FCSTD DOCUMENT  (FreeCAD 0.18R4 (GitTag))
Label: stator2
License: All rights reserved
LicenseURL: http://en.wikipedia.org/wiki/All_rights_reserved
objects: Sketcher::SketchObject×3, PartDesign::Body×2, Spreadsheet::Sheet×1
note: 5 computed .brp shape members not serialized (recipe doc carries the construction recipe); baked Part::Feature solids carry a one-line shape summary decoded from their .brp

FEATURE [Spreadsheet::Sheet] Spreadsheet  label="Variables"
  cells = A2=slotNumber; B2(slotNumber)=7; A3=outerDiameter; B3(outerDiameter)=50.15; A4=innerDiameter; B4(innerDiameter)=10; A5=stackLength; B5(stackLength)=20; A6=stackingFactor; B6(stackingFactor)=0.95; A7=cuttingThickness; B7(cuttingThickness)=0.1; A8=skewAngle; B8(skewAngle)=0; A9=segmentAngle; B9(segmentAngle)==360 / slotNumber; A10=tipHeightReduction; B10(tipHeightReduction)=50; A11=toothThickness; B11(toothThickness)=3; A12=yokeThickness; B12(yokeThickness)=4; A13=tipHeight; B13(tipHeight)=0.8; A14=tipAngle; B14(tipAngle)=90; A15=openingLeft; B15(openingLeft)=3; A16=openingRight; B16(openingRight)=3; A17=slotIsolation; B17(slotIsolation)=0.5; A18=windingAngle; B18(windingAngle)=35; A19=heightRatio; B19(heightRatio)=45; A20=roundingRadii; B20(roundingRadii)=0.2
FEATURE [Sketcher::SketchObject] Sketch003  label="StatorSegment"
  MapMode = 5
  Support = -> [XY_Plane]
  expr: Constraints[82] = Variables.roundingRadii
  expr: Constraints[54] = Variables.innerDiameter / 2 + Variables.yokeThickness
  expr: Constraints[79] = Variables.roundingRadii
  expr: Constraints[21] = 90
  expr: Constraints[64] = Variables.roundingRadii
  expr: Constraints[76] = Variables.roundingRadii
  expr: Constraints[42] = Variables.tipAngle
  expr: Constraints[13] = Variables.innerDiameter / 2
  expr: Constraints[7] = Variables.tipHeight
  expr: Constraints[27] = 90
  expr: Constraints[41] = Variables.tipAngle
  expr: Constraints[22] = Variables.openingLeft
  expr: Constraints[14] = Variables.segmentAngle / 2
  expr: Constraints[4] = Variables.tipHeight * (1 - Variables.tipHeightReduction / 100)
  expr: Constraints[89] = Variables.tipHeight
  expr: Constraints[32] = Variables.openingRight
  expr: Constraints[71] = Variables.roundingRadii
  expr: Constraints[46] = Variables.toothThickness / 2
  expr: Constraints[0] = Variables.segmentAngle
  expr: Constraints[18] = Variables.outerDiameter / 2
  expr: Constraints[34] = Variables.tipHeight * (1 - Variables.tipHeightReduction / 100)
  sketch-geometry (36):
    g0: LineSegment [constr] StartX=0 StartY=0 StartZ=0 EndX=15.634 EndY=19.6044 EndZ=0
    g1: LineSegment [constr] StartX=0 StartY=0 StartZ=0 EndX=25.075 EndY=0 EndZ=0
    g2: LineSegment [constr] StartX=0 StartY=0 StartZ=0 EndX=22.5918 EndY=10.8796 EndZ=0
    g3: LineSegment [constr] StartX=8.5045 StartY=23.7788 StartZ=0 EndX=21.2901 EndY=13.5825 EndZ=0
    g4: LineSegment [constr] StartX=21.2901 StartY=13.5825 StartZ=0 EndX=20.6826 EndY=13.29 EndZ=0
    g5: LineSegment [constr] StartX=20.5694 StartY=13.2354 StartZ=0 EndX=20.9298 EndY=13.409 EndZ=0
    g6: ArcOfCircle CenterX=2.20373 CenterY=2.76339 CenterZ=0 NormalX=0 NormalY=0 NormalZ=1 AngleXU=0 Radius=21.5405 StartAngle=0.51693 EndAngle=0.897598
    g7: LineSegment StartX=15.634 StartY=19.6044 StartZ=0 EndX=3.11745 EndY=3.90916 EndZ=0
    g8: ArcOfCircle CenterX=0 CenterY=0 CenterZ=0 NormalX=0 NormalY=0 NormalZ=1 AngleXU=0 Radius=5 StartAngle=0 EndAngle=0.897598
    g9: LineSegment [constr] StartX=22.5918 StartY=10.8796 StartZ=0 EndX=21.2901 EndY=13.5825 EndZ=0
    g10: LineSegment [constr] StartX=23.8934 StartY=8.17673 StartZ=0 EndX=23.1727 EndY=7.82962 EndZ=0
    g11: LineSegment [constr] StartX=22.5918 StartY=10.8796 StartZ=0 EndX=23.8934 EndY=8.17673 EndZ=0
    g12: LineSegment [constr] StartX=23.0594 StartY=7.7751 StartZ=0 EndX=23.4198 EndY=7.94865 EndZ=0
    g13: ArcOfCircle CenterX=5.1614 CenterY=0 CenterZ=0 NormalX=0 NormalY=0 NormalZ=1 AngleXU=0 Radius=19.9136 StartAngle=-9e-16 EndAngle=0.410597
    g14: LineSegment StartX=5 StartY=0 StartZ=0 EndX=25.075 EndY=0 EndZ=0
    g15: LineSegment StartX=20.4711 StartY=13.3138 StartZ=0 EndX=15.777 EndY=17.0572 EndZ=0
    g16: LineSegment StartX=15.496 StartY=17.0255 StartZ=0 EndX=7.02891 EndY=6.40816 EndZ=0
    g17: LineSegment StartX=7.00508 StartY=6.19668 StartZ=0 EndX=9.21236 EndY=1.61322 EndZ=0
    g18: LineSegment StartX=9.39255 StartY=1.5 StartZ=0 EndX=22.8594 EndY=1.5 EndZ=0
    g19: LineSegment StartX=23.0594 StartY=1.7 StartZ=0 EndX=23.0594 EndY=7.64943 EndZ=0
    g20: LineSegment [constr] StartX=7.02891 StartY=6.40816 StartZ=0 EndX=5.85616 EndY=7.34339 EndZ=0
    g21: LineSegment [constr] StartX=9.39255 StartY=1.5 StartZ=0 EndX=9.39255 EndY=0 EndZ=0
    g22: LineSegment [constr] StartX=0 StartY=0 StartZ=0 EndX=8.10872 EndY=3.90495 EndZ=0
    g23: LineSegment [constr] StartX=20.5694 StartY=13.2354 StartZ=0 EndX=20.9298 EndY=13.409 EndZ=0
    g24: LineSegment [constr] StartX=23.0594 StartY=7.7751 StartZ=0 EndX=23.4198 EndY=7.94865 EndZ=0
    g25: ArcOfCircle CenterX=20.5958 CenterY=13.4702 CenterZ=0 NormalX=0 NormalY=0 NormalZ=1 AngleXU=0 Radius=0.2 StartAngle=4.03919 EndAngle=5.16119
    g26: LineSegment [constr] StartX=20.4711 StartY=13.3138 StartZ=0 EndX=20.5694 EndY=13.2354 EndZ=0
    g27: ArcOfCircle CenterX=15.6523 CenterY=16.9008 CenterZ=0 NormalX=0 NormalY=0 NormalZ=1 AngleXU=0 Radius=0.2 StartAngle=0.897598 EndAngle=2.46839
    g28: ArcOfCircle CenterX=7.18527 CenterY=6.28346 CenterZ=0 NormalX=0 NormalY=0 NormalZ=1 AngleXU=0 Radius=0.2 StartAngle=2.46839 EndAngle=3.59039
    g29: ArcOfCircle CenterX=9.39255 CenterY=1.7 CenterZ=0 NormalX=0 NormalY=0 NormalZ=1 AngleXU=0 Radius=0.2 StartAngle=3.59039 EndAngle=4.71239
    g30: ArcOfCircle CenterX=22.8594 CenterY=1.7 CenterZ=0 NormalX=0 NormalY=0 NormalZ=1 AngleXU=0 Radius=0.2 StartAngle=4.71239 EndAngle=6.28319
    g31: ArcOfCircle CenterX=23.2594 CenterY=7.64943 CenterZ=0 NormalX=0 NormalY=0 NormalZ=1 AngleXU=0 Radius=0.2 StartAngle=2.0196 EndAngle=3.14159
    g32: LineSegment [constr] StartX=23.1727 StartY=7.82962 StartZ=0 EndX=23.0594 EndY=7.7751 EndZ=0
    g33: LineSegment [constr] StartX=23.0594 StartY=7.7751 StartZ=0 EndX=23.0594 EndY=7.64943 EndZ=0
    g34: LineSegment StartX=20.9298 StartY=13.409 StartZ=0 EndX=20.6826 EndY=13.29 EndZ=0
    g35: LineSegment StartX=23.1727 StartY=7.82962 StartZ=0 EndX=23.4198 EndY=7.94865 EndZ=0
  constraints (94):
    c: Angle(g1,g0) = 0.897598
    c: Symmetric(g3,g3,g0)
    c: Coincident(g4,g3)
    c: PointOnObject(g5,g4)
    c: Distance(g5) = 0.4
    c: Coincident(g6,g5)
    c: PointOnObject(g6,g0)
    c: Distance(g5,g3) = 0.8
    c: Coincident(g7,g6)
    c: PointOnObject(g7,g0)
    c: PointOnObject(g8,g1)
    c: Coincident(g8,g-1)
    c: Coincident(g8,g7)
    c: Radius(g8) = 5
    c: Angle(g-1,g2) = 0.448799
    c: Angle(g-1,g1) = 0
    c: Coincident(g2,g8)
    c: Coincident(g0,g8)
    c: Distance(g2) = 25.075
    c: Coincident(g9,g2)
    c: Coincident(g9,g3)
    c: Angle(g9,g2) = 1.5708
    c: Distance(g9) = 3
    c: Coincident(g6,g0)
    c: Equal(g0,g2)
    c: Equal(g1,g2)
    c: Coincident(g1,g8)
    c: Angle(g4,g9) = 1.5708
    c: Coincident(g11,g2)
    c: Coincident(g11,g10)
    c: Angle(g2,g11) = 1.5708
    c: Angle(g11,g10) = 1.5708
    c: Distance(g11) = 3
    c: Angle(g10,g12) = 0
    c: Distance(g12,g12) = 0.4
    c: PointOnObject(g13,g1)
    c: Coincident(g13,g12)
    c: Coincident(g13,g1)
    c: Coincident(g14,g8)
    c: Coincident(g14,g13)
    c: Horizontal(g18)
    c: Angle(g16,g15) = 1.5708
    c: Angle(g19,g18) = 1.5708
    c: PointOnObject(g20,g7)
    c: Angle(g16,g20) = 1.5708
    c: Angle(g20,g0) = 1.5708
    c: Distance(g20) = 1.5
    c: PointOnObject(g21,g14)
    c: Angle(g21,g18) = 1.5708
    c: Equal(g21,g20)
    c: Coincident(g22,g8)
    c: PointOnObject(g22,g17)
    c: Angle(g17,g22) = 1.5708
    c: PointOnObject(g22,g2)
    c: Distance(g8,g22) = 9
    c: Coincident(g23,g5)
    c: Coincident(g23,g6)
    c: Coincident(g24,g12)
    c: Coincident(g24,g13)
    c: Tangent(g4,g25) = 1.5708
    c: Tangent(g15,g25) = 1.5708
    c: Coincident(g26,g15)
    c: Coincident(g26,g5)
    c: Parallel(g26,g15)
    c: Radius(g25) = 0.2
    c: PointOnObject(g4,g5)
    c: Tangent(g16,g27) = -1.5708
    c: Tangent(g15,g27) = -1.5708
    c: Equal(g27,g25)
    c: Tangent(g17,g28) = -1.5708
    c: Tangent(g16,g28) = -1.5708
    c: Radius(g28) = 0.2
    c: Coincident(g20,g16)
    c: Tangent(g17,g29) = -1.5708
    c: Tangent(g18,g29) = -1.5708
    c: Coincident(g21,g18)
    c: Radius(g29) = 0.2
    c: Tangent(g18,g30) = -1.5708
    c: Tangent(g19,g30) = -1.5708
    c: Radius(g30) = 0.2
    c: Tangent(g19,g31) = 1.5708
    c: Tangent(g10,g31) = -1.5708
    c: Radius(g31) = 0.2
    c: Coincident(g32,g10)
    c: Coincident(g33,g32)
    c: Coincident(g33,g19)
    c: Parallel(g19,g33)
    c: Parallel(g32,g10)
    c: Coincident(g12,g32)
    c: Distance(g10) = 0.8
    c: Coincident(g34,g6)
    c: Coincident(g34,g4)
    c: Coincident(g35,g31)
    c: Coincident(g35,g13)
FEATURE [Sketcher::SketchObject] Sketch  label="StatorStack"
  MapMode = 5
  Support = -> [XY_Plane001]
  expr: Constraints[20] = Variables.innerDiameter / 2
  expr: Constraints[10] = Variables.outerDiameter / 2
  expr: Constraints[9] = Variables.innerDiameter / 2
  expr: Constraints[8] = Variables.stackLength
  sketch-geometry (8):
    g0: LineSegment StartX=-10 StartY=5 StartZ=0 EndX=10 EndY=5 EndZ=0
    g1: LineSegment StartX=10 StartY=5 StartZ=0 EndX=10 EndY=25.075 EndZ=0
    g2: LineSegment StartX=10 StartY=25.075 StartZ=0 EndX=-10 EndY=25.075 EndZ=0
    g3: LineSegment StartX=-10 StartY=25.075 StartZ=0 EndX=-10 EndY=5 EndZ=0
    g4: LineSegment StartX=-10 StartY=-5 StartZ=0 EndX=10 EndY=-5 EndZ=0
    g5: LineSegment StartX=10 StartY=-5 StartZ=0 EndX=10 EndY=-25.075 EndZ=0
    g6: LineSegment StartX=10 StartY=-25.075 StartZ=0 EndX=-10 EndY=-25.075 EndZ=0
    g7: LineSegment StartX=-10 StartY=-25.075 StartZ=0 EndX=-10 EndY=-5 EndZ=0
  constraints (22):
    c: Coincident(g0,g1)
    c: Coincident(g1,g2)
    c: Coincident(g2,g3)
    c: Coincident(g3,g0)
    c: Horizontal(g2)
    c: Vertical(g1)
    c: Vertical(g3)
    c: Symmetric(g0,g0,g-2)
    c: DistanceX(g0,g0) = 20
    c: DistanceY(g-1,g0) = 5
    c: DistanceY(g-1,g1) = 25.075
    c: Coincident(g4,g5)
    c: Coincident(g5,g6)
    c: Coincident(g6,g7)
    c: Coincident(g7,g4)
    c: Horizontal(g6)
    c: Vertical(g5)
    c: Vertical(g7)
    c: Equal(g4,g0)
    c: Symmetric(g4,g4,g-2)
    c: DistanceY(g4,g-1) = 5
    c: Equal(g7,g3)
FEATURE [PartDesign::Body] Body001  label="SideView"
  Group = -> [Sketch]
  Origin = -> Origin001
FEATURE [Sketcher::SketchObject] Sketch004  label="Slot"
  MapMode = 5
  Support = -> [XY_Plane]
  expr: Constraints[82] = Variables.roundingRadii
  expr: Constraints[79] = Variables.roundingRadii
  expr: Constraints[54] = Variables.innerDiameter / 2 + Variables.yokeThickness
  expr: Constraints[21] = 90
  expr: Constraints[64] = Variables.roundingRadii
  expr: Constraints[76] = Variables.roundingRadii
  expr: Constraints[42] = Variables.tipAngle
  expr: Constraints[13] = Variables.innerDiameter / 2
  expr: Constraints[7] = Variables.tipHeight
  expr: Constraints[27] = 90
  expr: Constraints[41] = Variables.tipAngle
  expr: Constraints[22] = Variables.openingLeft
  expr: Constraints[14] = Variables.segmentAngle / 2
  expr: Constraints[4] = Variables.tipHeight * (1 - Variables.tipHeightReduction / 100)
  expr: Constraints[89] = Variables.tipHeight
  expr: Constraints[32] = Variables.openingRight
  expr: Constraints[71] = Variables.roundingRadii
  expr: Constraints[46] = Variables.toothThickness / 2
  expr: Constraints[34] = Variables.tipHeight * (1 - Variables.tipHeightReduction / 100)
  expr: Constraints[18] = Variables.outerDiameter / 2
  expr: Constraints[0] = Variables.segmentAngle
  sketch-geometry (37):
    g0: LineSegment [constr] StartX=0 StartY=0 StartZ=0 EndX=15.634 EndY=19.6044 EndZ=0
    g1: LineSegment [constr] StartX=0 StartY=0 StartZ=0 EndX=25.075 EndY=0 EndZ=0
    g2: LineSegment [constr] StartX=0 StartY=0 StartZ=0 EndX=22.5918 EndY=10.8796 EndZ=0
    g3: LineSegment [constr] StartX=8.5045 StartY=23.7788 StartZ=0 EndX=21.2901 EndY=13.5825 EndZ=0
    g4: LineSegment [constr] StartX=21.2901 StartY=13.5825 StartZ=0 EndX=20.6826 EndY=13.29 EndZ=0
    g5: LineSegment [constr] StartX=20.5694 StartY=13.2354 StartZ=0 EndX=20.9298 EndY=13.409 EndZ=0
    g6: ArcOfCircle [constr] CenterX=2.20373 CenterY=2.76339 CenterZ=0 NormalX=0 NormalY=0 NormalZ=1 AngleXU=0 Radius=21.5405 StartAngle=0.51693 EndAngle=0.897598
    g7: LineSegment [constr] StartX=15.634 StartY=19.6044 StartZ=0 EndX=3.11745 EndY=3.90916 EndZ=0
    g8: ArcOfCircle [constr] CenterX=0 CenterY=0 CenterZ=0 NormalX=0 NormalY=0 NormalZ=1 AngleXU=0 Radius=5 StartAngle=0 EndAngle=0.897598
    g9: LineSegment [constr] StartX=22.5918 StartY=10.8796 StartZ=0 EndX=21.2901 EndY=13.5825 EndZ=0
    g10: LineSegment [constr] StartX=23.8934 StartY=8.17673 StartZ=0 EndX=23.1727 EndY=7.82962 EndZ=0
    g11: LineSegment [constr] StartX=22.5918 StartY=10.8796 StartZ=0 EndX=23.8934 EndY=8.17673 EndZ=0
    g12: LineSegment [constr] StartX=23.0594 StartY=7.7751 StartZ=0 EndX=23.4198 EndY=7.94865 EndZ=0
    g13: ArcOfCircle [constr] CenterX=5.1614 CenterY=0 CenterZ=0 NormalX=0 NormalY=0 NormalZ=1 AngleXU=0 Radius=19.9136 StartAngle=0 EndAngle=0.410597
    g14: LineSegment [constr] StartX=5 StartY=0 StartZ=0 EndX=25.075 EndY=0 EndZ=0
    g15: LineSegment StartX=20.4711 StartY=13.3138 StartZ=0 EndX=15.777 EndY=17.0572 EndZ=0
    g16: LineSegment StartX=15.496 StartY=17.0255 StartZ=0 EndX=7.02891 EndY=6.40816 EndZ=0
    g17: LineSegment StartX=7.00508 StartY=6.19668 StartZ=0 EndX=9.21236 EndY=1.61322 EndZ=0
    g18: LineSegment StartX=9.39255 StartY=1.5 StartZ=0 EndX=22.8594 EndY=1.5 EndZ=0
    g19: LineSegment StartX=23.0594 StartY=1.7 StartZ=0 EndX=23.0594 EndY=7.64943 EndZ=0
    g20: LineSegment [constr] StartX=7.02891 StartY=6.40816 StartZ=0 EndX=5.85616 EndY=7.34339 EndZ=0
    g21: LineSegment [constr] StartX=9.39255 StartY=1.5 StartZ=0 EndX=9.39255 EndY=0 EndZ=0
    g22: LineSegment [constr] StartX=0 StartY=0 StartZ=0 EndX=8.10872 EndY=3.90495 EndZ=0
    g23: LineSegment [constr] StartX=20.5694 StartY=13.2354 StartZ=0 EndX=20.9298 EndY=13.409 EndZ=0
    g24: LineSegment [constr] StartX=23.0594 StartY=7.7751 StartZ=0 EndX=23.4198 EndY=7.94865 EndZ=0
    g25: ArcOfCircle CenterX=20.5958 CenterY=13.4702 CenterZ=0 NormalX=0 NormalY=0 NormalZ=1 AngleXU=0 Radius=0.2 StartAngle=4.03919 EndAngle=5.16119
    g26: LineSegment [constr] StartX=20.4711 StartY=13.3138 StartZ=0 EndX=20.5694 EndY=13.2354 EndZ=0
    g27: ArcOfCircle CenterX=15.6523 CenterY=16.9008 CenterZ=0 NormalX=0 NormalY=0 NormalZ=1 AngleXU=0 Radius=0.2 StartAngle=0.897598 EndAngle=2.46839
    g28: ArcOfCircle CenterX=7.18527 CenterY=6.28346 CenterZ=0 NormalX=0 NormalY=0 NormalZ=1 AngleXU=0 Radius=0.2 StartAngle=2.46839 EndAngle=3.59039
    g29: ArcOfCircle CenterX=9.39255 CenterY=1.7 CenterZ=0 NormalX=0 NormalY=0 NormalZ=1 AngleXU=0 Radius=0.2 StartAngle=3.59039 EndAngle=4.71239
    g30: ArcOfCircle CenterX=22.8594 CenterY=1.7 CenterZ=0 NormalX=0 NormalY=0 NormalZ=1 AngleXU=0 Radius=0.2 StartAngle=4.71239 EndAngle=6.28319
    g31: ArcOfCircle CenterX=23.2594 CenterY=7.64943 CenterZ=0 NormalX=0 NormalY=0 NormalZ=1 AngleXU=0 Radius=0.2 StartAngle=2.0196 EndAngle=3.14159
    g32: LineSegment [constr] StartX=23.1727 StartY=7.82962 StartZ=0 EndX=23.0594 EndY=7.7751 EndZ=0
    g33: LineSegment [constr] StartX=23.0594 StartY=7.7751 StartZ=0 EndX=23.0594 EndY=7.64943 EndZ=0
    g34: LineSegment StartX=20.9298 StartY=13.409 StartZ=0 EndX=20.6826 EndY=13.29 EndZ=0
    g35: LineSegment StartX=23.1727 StartY=7.82962 StartZ=0 EndX=23.4198 EndY=7.94865 EndZ=0
    g36: LineSegment StartX=20.9298 StartY=13.409 StartZ=0 EndX=23.4198 EndY=7.94865 EndZ=0
  constraints (96):
    c: Angle(g1,g0) = 0.897598
    c: Symmetric(g3,g3,g0)
    c: Coincident(g4,g3)
    c: PointOnObject(g5,g4)
    c: Distance(g5) = 0.4
    c: Coincident(g6,g5)
    c: PointOnObject(g6,g0)
    c: Distance(g5,g3) = 0.8
    c: Coincident(g7,g6)
    c: PointOnObject(g7,g0)
    c: PointOnObject(g8,g1)
    c: Coincident(g8,g-1)
    c: Coincident(g8,g7)
    c: Radius(g8) = 5
    c: Angle(g-1,g2) = 0.448799
    c: Angle(g-1,g1) = 0
    c: Coincident(g2,g8)
    c: Coincident(g0,g8)
    c: Distance(g2) = 25.075
    c: Coincident(g9,g2)
    c: Coincident(g9,g3)
    c: Angle(g9,g2) = 1.5708
    c: Distance(g9) = 3
    c: Coincident(g6,g0)
    c: Equal(g0,g2)
    c: Equal(g1,g2)
    c: Coincident(g1,g8)
    c: Angle(g4,g9) = 1.5708
    c: Coincident(g11,g2)
    c: Coincident(g11,g10)
    c: Angle(g2,g11) = 1.5708
    c: Angle(g11,g10) = 1.5708
    c: Distance(g11) = 3
    c: Angle(g10,g12) = 0
    c: Distance(g12,g12) = 0.4
    c: PointOnObject(g13,g1)
    c: Coincident(g13,g12)
    c: Coincident(g13,g1)
    c: Coincident(g14,g8)
    c: Coincident(g14,g13)
    c: Horizontal(g18)
    c: Angle(g16,g15) = 1.5708
    c: Angle(g19,g18) = 1.5708
    c: PointOnObject(g20,g7)
    c: Angle(g16,g20) = 1.5708
    c: Angle(g20,g0) = 1.5708
    c: Distance(g20) = 1.5
    c: PointOnObject(g21,g14)
    c: Angle(g21,g18) = 1.5708
    c: Equal(g21,g20)
    c: Coincident(g22,g8)
    c: PointOnObject(g22,g17)
    c: Angle(g17,g22) = 1.5708
    c: PointOnObject(g22,g2)
    c: Distance(g8,g22) = 9
    c: Coincident(g23,g5)
    c: Coincident(g23,g6)
    c: Coincident(g24,g12)
    c: Coincident(g24,g13)
    c: Tangent(g4,g25) = 1.5708
    c: Tangent(g15,g25) = 1.5708
    c: Coincident(g26,g15)
    c: Coincident(g26,g5)
    c: Parallel(g26,g15)
    c: Radius(g25) = 0.2
    c: PointOnObject(g4,g5)
    c: Tangent(g16,g27) = -1.5708
    c: Tangent(g15,g27) = -1.5708
    c: Equal(g27,g25)
    c: Tangent(g17,g28) = -1.5708
    c: Tangent(g16,g28) = -1.5708
    c: Radius(g28) = 0.2
    c: Coincident(g20,g16)
    c: Tangent(g17,g29) = -1.5708
    c: Tangent(g18,g29) = -1.5708
    c: Coincident(g21,g18)
    c: Radius(g29) = 0.2
    c: Tangent(g18,g30) = -1.5708
    c: Tangent(g19,g30) = -1.5708
    c: Radius(g30) = 0.2
    c: Tangent(g19,g31) = 1.5708
    c: Tangent(g10,g31) = -1.5708
    c: Radius(g31) = 0.2
    c: Coincident(g32,g10)
    c: Coincident(g33,g32)
    c: Coincident(g33,g19)
    c: Parallel(g19,g33)
    c: Parallel(g32,g10)
    c: Coincident(g12,g32)
    c: Distance(g10) = 0.8
    c: Coincident(g34,g6)
    c: Coincident(g34,g4)
    c: Coincident(g35,g31)
    c: Coincident(g35,g13)
    c: Coincident(g36,g34)
    c: Coincident(g36,g35)
FEATURE [PartDesign::Body] Body  label="TopView"
  Group = -> [Sketch003,Sketch004]
  Origin = -> Origin
